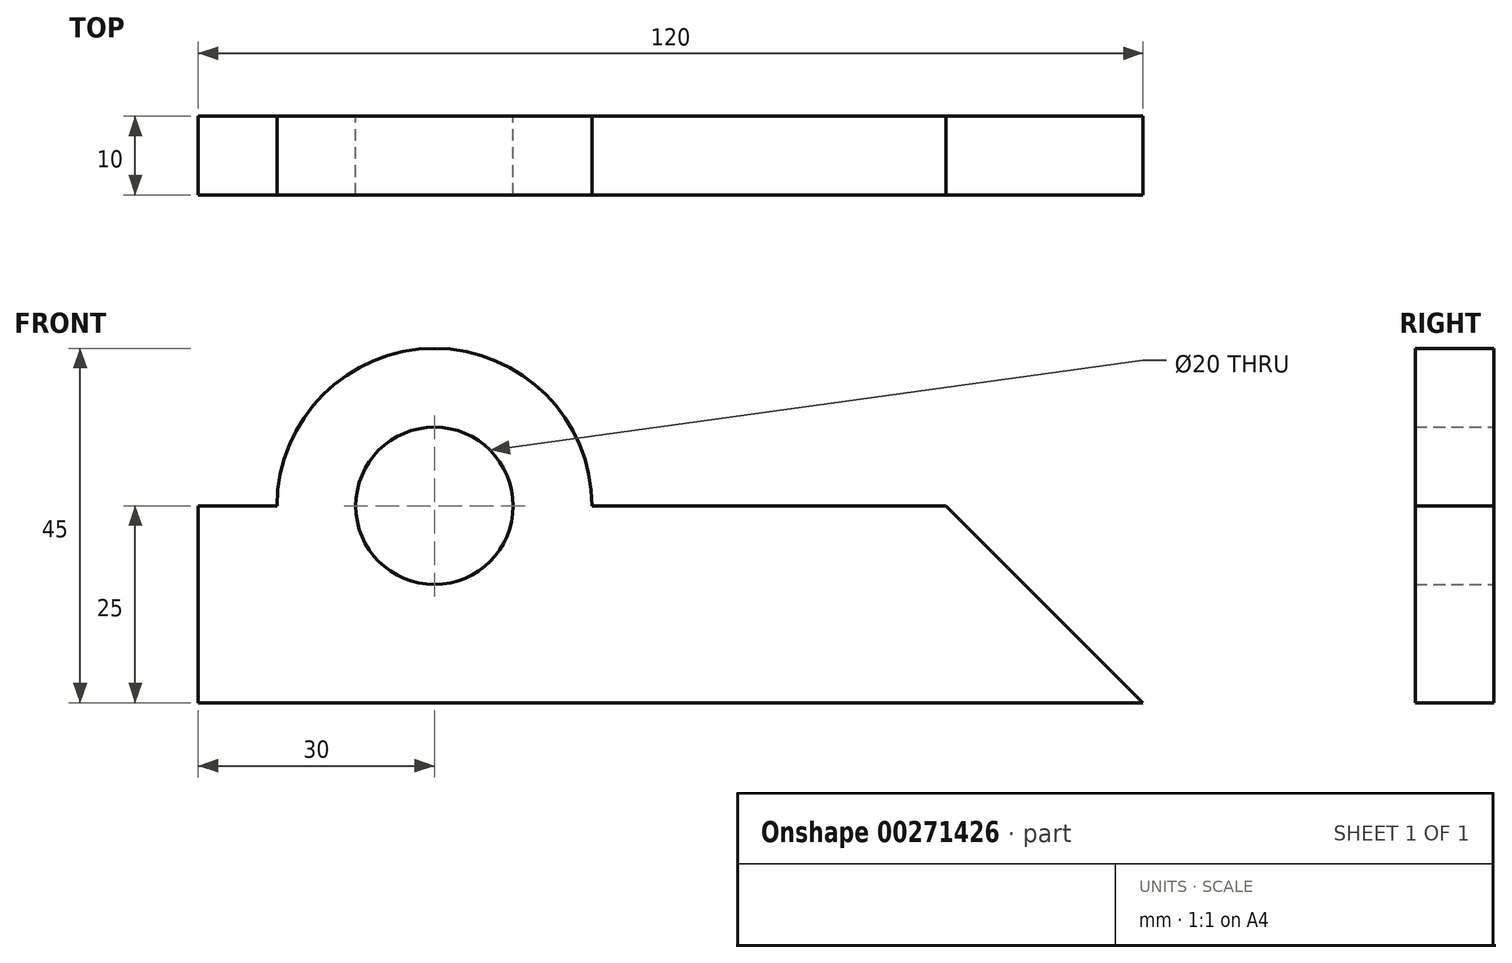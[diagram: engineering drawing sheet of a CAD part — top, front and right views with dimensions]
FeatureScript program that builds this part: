
annotation { "Feature Type Name" : "Feature", "Feature Type Description" : "" }
export const myFeature = defineFeature(function(context is Context, id is Id, definition is map)
    precondition{}
    {
        {
            var Q0;
            Q0=qCreatedBy(makeId("Front.planeOp"),FACE);
            var sketch = newSketch(context, id + "F0", { "sketchPlane" : qUnion([Q0])});
            skLineSegment(sketch, "E0", {"start": v(0, 0) * mm, "end": v(0, 25) * mm});
            skLineSegment(sketch, "E1", {"start": v(0, 0) * mm, "end": v(120, 0) * mm});
            skLineSegment(sketch, "E2", {"start": v(120, 0) * mm, "end": v(95, 25) * mm});
            skLineSegment(sketch, "E3", {"start": v(95, 25) * mm, "end": v(50, 25) * mm});
            skCircle(sketch, "E4", {"center": v(30, 25) * mm, "radius": 10 * mm});
            skLineSegment(sketch, "E5", {"start": v(0, 25) * mm, "end": v(10, 25) * mm});
            skArc(sketch, "E6", {"start": v(50, 25) * mm, "mid": v(30, 45) * mm, "end": v(10, 25) * mm});
            skSolve(sketch);
        }
        {
            var Q0;
            Q0 = qSketchRegion(id + "F0", true);
            extrude(context, id + "F1", {"entities" : qUnion([Q0]), "depth" : 10 * mm});
        }
    });
